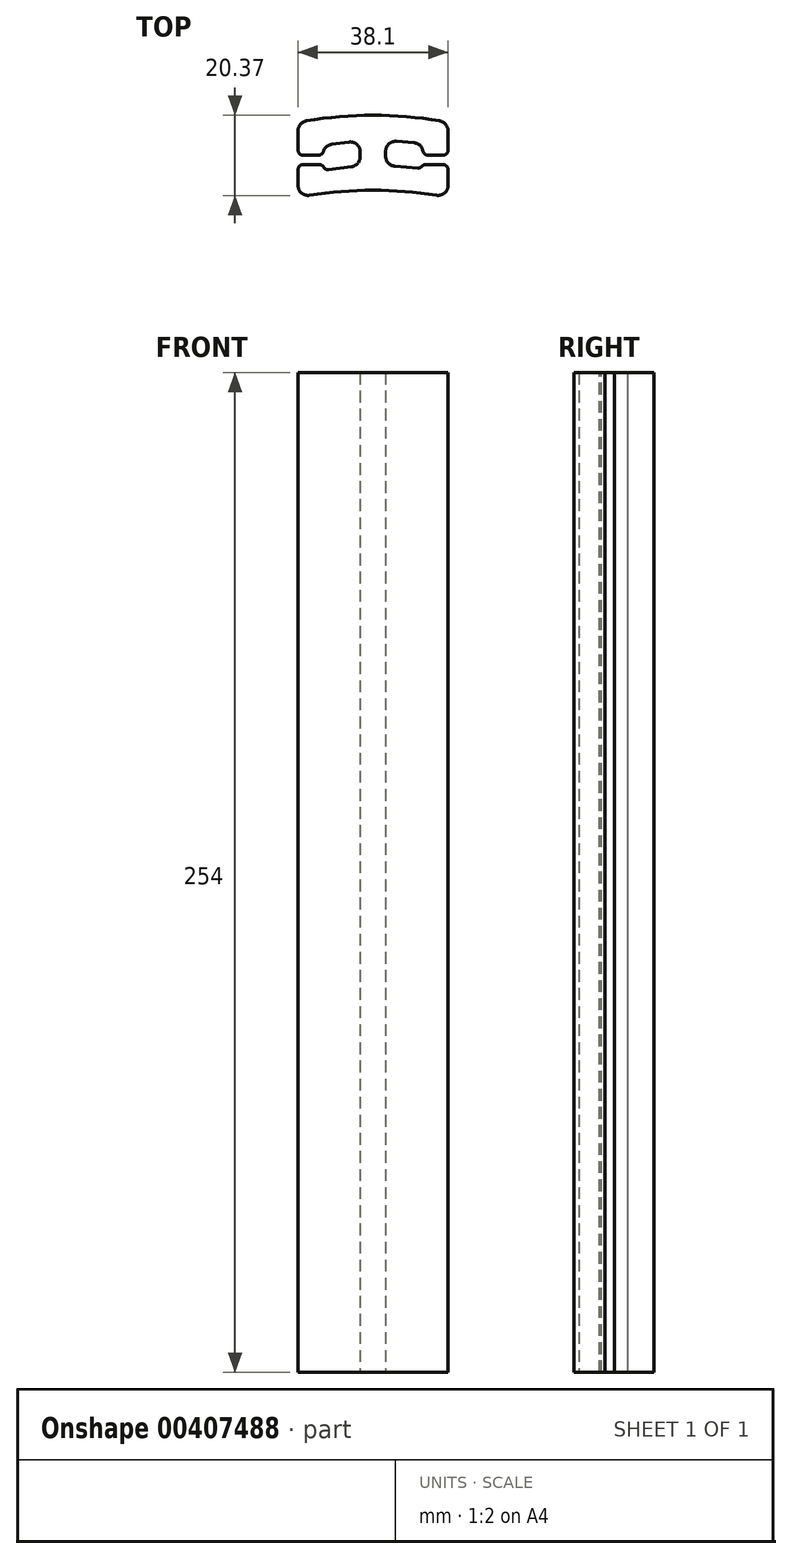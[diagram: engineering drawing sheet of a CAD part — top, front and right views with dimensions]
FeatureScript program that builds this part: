
annotation { "Feature Type Name" : "Feature", "Feature Type Description" : "" }
export const myFeature = defineFeature(function(context is Context, id is Id, definition is map)
    precondition{}
    {
        {
            var Q0;
            Q0=qCreatedBy(makeId("Top.planeOp"),FACE);
            var sketch = newSketch(context, id + "F0", { "sketchPlane" : qUnion([Q0])});
            skLineSegment(sketch, "E0.left", {"start": v(19.05, -9.52) * mm, "end": v(19.05, -1.2) * mm});
            skLineSegment(sketch, "E0.right", {"start": v(-19.05, -9.53) * mm, "end": v(-19.05, -1.2) * mm});
            skPoint(sketch, "E0.middle", {"position": v(0, 0) * mm});
            skLineSegment(sketch, "E1", {"start": v(-19.05, 1.2) * mm, "end": v(-12.7, 1.2) * mm});
            skLineSegment(sketch, "E2", {"start": v(-19.05, -1.2) * mm, "end": v(-12.7, -1.2) * mm});
            skLineSegment(sketch, "E3.trimOffspring", {"start": v(-19.05, 1.2) * mm, "end": v(-19.05, 9.52) * mm});
            skLineSegment(sketch, "E4", {"start": v(0, -9.53) * mm, "end": v(0, -7.72) * mm});
            skLineSegment(sketch, "E5", {"start": v(12.7, -1.2) * mm, "end": v(19.05, -1.2) * mm});
            skLineSegment(sketch, "E6.trimOffspring", {"start": v(19.05, 1.2) * mm, "end": v(19.05, 9.53) * mm});
            skLineSegment(sketch, "E7", {"start": v(12.7, 1) * mm, "end": v(12.7, 1.2) * mm});
            skLineSegment(sketch, "E8", {"start": v(19.05, 1.2) * mm, "end": v(12.7, 1.2) * mm});
            skArc(sketch, "E9", {"start": v(19.05, 9.52) * mm, "mid": v(0, 11.33) * mm, "end": v(-19.05, 9.52) * mm});
            skArc(sketch, "E10", {"start": v(19.05, -9.52) * mm, "mid": v(0, -7.72) * mm, "end": v(-19.05, -9.52) * mm});
            skPoint(sketch, "E11.orphan", {"position": v(0, 9.53) * mm});
            skPoint(sketch, "E12.orphan", {"position": v(19.05, 0) * mm});
            skPoint(sketch, "E13.orphan", {"position": v(-19.05, 0) * mm});
            skLineSegment(sketch, "E14", {"start": v(-12.7, 1.2) * mm, "end": v(-12.7, 3.65) * mm});
            skLineSegment(sketch, "E15", {"start": v(-12.7, 3.65) * mm, "end": v(-3.26, 4.92) * mm});
            skLineSegment(sketch, "E16", {"start": v(-12.7, -1.2) * mm, "end": v(-12.7, -2.7) * mm});
            skLineSegment(sketch, "E17", {"start": v(-12.7, -2.7) * mm, "end": v(-3.26, -1.43) * mm});
            skLineSegment(sketch, "E18", {"start": v(-3.26, 4.92) * mm, "end": v(-3.26, 1.75) * mm});
            skLineSegment(sketch, "E19", {"start": v(-3.26, -1.43) * mm, "end": v(-3.26, 1.75) * mm});
            skLineSegment(sketch, "E20", {"start": v(12.7, 1) * mm, "end": v(12.7, 4.18) * mm});
            skLineSegment(sketch, "E21", {"start": v(12.7, 4.18) * mm, "end": v(12.7, 1) * mm});
            skLineSegment(sketch, "E22", {"start": v(12.7, -1.2) * mm, "end": v(12.7, -2.17) * mm});
            skLineSegment(sketch, "E23", {"start": v(12.7, 4.18) * mm, "end": v(3.2, 4.93) * mm});
            skLineSegment(sketch, "E24", {"start": v(3.2, 4.93) * mm, "end": v(3.2, 1.75) * mm});
            skLineSegment(sketch, "E25", {"start": v(3.2, 1.75) * mm, "end": v(3.2, -1.42) * mm});
            skLineSegment(sketch, "E26", {"start": v(3.2, -1.42) * mm, "end": v(12.7, -2.17) * mm});
            skSolve(sketch);
        }
        {
            var Q0;
            Q0 = qSketchRegion(id + "F0", true);
            extrude(context, id + "F1", {"entities" : qUnion([Q0]), "depth" : 254 * mm});
        }
        {
            var Q0;
            Q0=makeQuery(id+"F1.opExtrude","SWEPT_EDGE",EDGE,{"disambiguationData":[OSD([sQuery(id+"F0.wireOp",EDGE,"E0.left"),sQuery(id+"F0.wireOp",EDGE,"E10")])]});
            var Q1;
            Q1=makeQuery(id+"F1.opExtrude","SWEPT_EDGE",EDGE,{"disambiguationData":[OSD([sQuery(id+"F0.wireOp",EDGE,"E6.trimOffspring"),sQuery(id+"F0.wireOp",EDGE,"E9")])]});
            var Q2;
            Q2=makeQuery(id+"F1.opExtrude","SWEPT_EDGE",EDGE,{"disambiguationData":[OSD([sQuery(id+"F0.wireOp",EDGE,"E0.right"),sQuery(id+"F0.wireOp",EDGE,"E10")])]});
            var Q3;
            Q3=makeQuery(id+"F1.opExtrude","SWEPT_EDGE",EDGE,{"disambiguationData":[OSD([sQuery(id+"F0.wireOp",EDGE,"E3.trimOffspring"),sQuery(id+"F0.wireOp",EDGE,"E9")])]});
            var Q4;
            Q4=makeQuery(id+"F1.opExtrude","SWEPT_EDGE",EDGE,{"disambiguationData":[OSD([sQuery(id+"F0.wireOp",EDGE,"E14"),sQuery(id+"F0.wireOp",EDGE,"E15")])]});
            var Q5;
            Q5=makeQuery(id+"F1.opExtrude","SWEPT_EDGE",EDGE,{"disambiguationData":[OSD([sQuery(id+"F0.wireOp",EDGE,"E23"),sQuery(id+"F0.wireOp",EDGE,"E24")])]});
            var Q6;
            Q6=makeQuery(id+"F1.opExtrude","SWEPT_EDGE",EDGE,{"disambiguationData":[OSD([sQuery(id+"F0.wireOp",EDGE,"E25"),sQuery(id+"F0.wireOp",EDGE,"E26")])]});
            var Q7;
            Q7=makeQuery(id+"F1.opExtrude","SWEPT_EDGE",EDGE,{"disambiguationData":[OSD([sQuery(id+"F0.wireOp",EDGE,"E21"),sQuery(id+"F0.wireOp",EDGE,"E23")])]});
            var Q8;
            Q8=makeQuery(id+"F1.opExtrude","SWEPT_EDGE",EDGE,{"disambiguationData":[OSD([sQuery(id+"F0.wireOp",EDGE,"E15"),sQuery(id+"F0.wireOp",EDGE,"E18")])]});
            var Q9;
            Q9=makeQuery(id+"F1.opExtrude","SWEPT_EDGE",EDGE,{"disambiguationData":[OSD([sQuery(id+"F0.wireOp",EDGE,"E17"),sQuery(id+"F0.wireOp",EDGE,"E19")])]});
            fillet(context, id + "F2", {"entities" : qUnion([Q0, Q1, Q2, Q3, Q4, Q5, Q6, Q7, Q8, Q9]), "radius" : 2.54 * mm, "tangentPropagation" : true, "allowEdgeOverflow" : false});
        }
        {
            var Q0;
            Q0=makeQuery(id+"F1.opExtrude","SWEPT_EDGE",EDGE,{"disambiguationData":[OSD([sQuery(id+"F0.wireOp",EDGE,"E0.left"),sQuery(id+"F0.wireOp",EDGE,"E5")])]});
            var Q1;
            Q1=makeQuery(id+"F1.opExtrude","SWEPT_EDGE",EDGE,{"disambiguationData":[OSD([sQuery(id+"F0.wireOp",EDGE,"E6.trimOffspring"),sQuery(id+"F0.wireOp",EDGE,"E8")])]});
            var Q2;
            Q2=makeQuery(id+"F1.opExtrude","SWEPT_EDGE",EDGE,{"disambiguationData":[OSD([sQuery(id+"F0.wireOp",EDGE,"E0.right"),sQuery(id+"F0.wireOp",EDGE,"E2")])]});
            var Q3;
            Q3=makeQuery(id+"F1.opExtrude","SWEPT_EDGE",EDGE,{"disambiguationData":[OSD([sQuery(id+"F0.wireOp",EDGE,"E1"),sQuery(id+"F0.wireOp",EDGE,"E3.trimOffspring")])]});
            fillet(context, id + "F3", {"entities" : qUnion([Q0, Q1, Q2, Q3]), "radius" : 1.27 * mm, "tangentPropagation" : true, "allowEdgeOverflow" : false});
        }
        {
            var Q0;
            Q0=makeQuery(id+"F1.opExtrude","SWEPT_EDGE",EDGE,{"disambiguationData":[OSD([sQuery(id+"F0.wireOp",EDGE,"E22"),sQuery(id+"F0.wireOp",EDGE,"E26")])]});
            fillet(context, id + "F4", {"entities" : qUnion([Q0]), "radius" : 1.27 * mm, "tangentPropagation" : true, "allowEdgeOverflow" : false});
        }
        {
            var Q0;
            Q0=makeQuery(id+"F1.opExtrude","SWEPT_EDGE",EDGE,{"disambiguationData":[OSD([sQuery(id+"F0.wireOp",EDGE,"E16"),sQuery(id+"F0.wireOp",EDGE,"E17")])]});
            fillet(context, id + "F5", {"entities" : qUnion([Q0]), "radius" : 1.27 * mm, "tangentPropagation" : true, "allowEdgeOverflow" : false});
        }
        {
            var Q0;
            Q0=makeQuery(id+"F1.opExtrude","SWEPT_EDGE",EDGE,{"disambiguationData":[OSD([sQuery(id+"F0.wireOp",EDGE,"E1"),sQuery(id+"F0.wireOp",EDGE,"E14")])]});
            var Q1;
            Q1=makeQuery(id+"F1.opExtrude","SWEPT_EDGE",EDGE,{"disambiguationData":[OSD([sQuery(id+"F0.wireOp",EDGE,"E2"),sQuery(id+"F0.wireOp",EDGE,"E16")])]});
            var Q2;
            Q2=makeQuery(id+"F1.opExtrude","SWEPT_EDGE",EDGE,{"disambiguationData":[OSD([sQuery(id+"F0.wireOp",EDGE,"E8"),sQuery(id+"F0.wireOp",EDGE,"E21")])]});
            fillet(context, id + "F6", {"entities" : qUnion([Q0, Q1, Q2]), "radius" : 1.27 * mm, "tangentPropagation" : true, "allowEdgeOverflow" : false});
        }
        {
            var Q0;
            Q0=makeQuery(id+"F4.opFillet","BLEND_EDGE",EDGE,{"blendedFrom":[makeQuery(id+"F1.opExtrude","SWEPT_EDGE",EDGE,{"disambiguationData":[OSD([sQuery(id+"F0.wireOp",EDGE,"E22"),sQuery(id+"F0.wireOp",EDGE,"E26")])]}),makeQuery(id+"F1.opExtrude","SWEPT_FACE",FACE,{"disambiguationData":[OSD([sQuery(id+"F0.wireOp",EDGE,"E5")])]})],"blendedInto":[makeQuery(id+"F1.opExtrude","SWEPT_FACE",FACE,{"disambiguationData":[OSD([sQuery(id+"F0.wireOp",EDGE,"E5")])]})]});
            fillet(context, id + "F7", {"entities" : qUnion([Q0]), "radius" : 1.27 * mm, "tangentPropagation" : true, "allowEdgeOverflow" : false});
        }
    });
